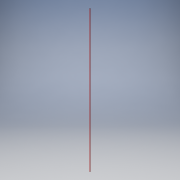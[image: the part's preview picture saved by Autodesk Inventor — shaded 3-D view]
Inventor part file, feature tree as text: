
AUTODESK INVENTOR PART (.ipt)
format: ipt  version: 2016 (Build 200138000, 138)  size: 103,424 bytes
history: native  units: in
note: dims shown in document units (in); Inventor stores cm internally (conversion verified against a paired STEP export)
features: extrude x1, sketch x1
ambient origin geometry x8: Origin, YZ Plane, XZ Plane, XY Plane, X Axis, Y Axis, Z Axis, Center Point
bodies: Solid1 (feature_tree)
feature tree (2):
  extrude  "Extrusion1"  Depth=117.126in TaperAngle=0.0deg
  sketch  "Sketch1"  dims[d0=0.3937in d1=117.126in d2=0.0in]
